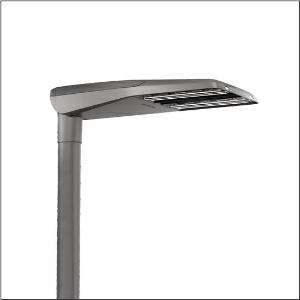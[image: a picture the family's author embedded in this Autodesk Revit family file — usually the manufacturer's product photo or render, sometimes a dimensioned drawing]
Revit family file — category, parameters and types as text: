
# Revit family: streetlight_sl_11_iq_midi___st1_2a_5xc3a51f08me_8c89
name_source: partatom
category: Lighting Fixtures
units: mm (PartAtom-declared; Revit-internal decimal feet)

## family parameters
Cut with Voids When Loaded = No
Host = Face
Light Source = No
Part Type = Normal
Room Calculation Point = No
Round Connector Dimension = Use Diameter
Shared = No

## types (1)
- --- (1 x LED, 18110 lm, 124.7 W, 3000K)
    Apparent Load = 125 VA
    CIE Flux Codes = 32 70 96 100 100
    Color Rendering = 70
    Color Temperature = 3000K
    Default Elevation = 1800 mm
    Description = Streetlight SL 11 iQ midi, mast luminaire, primary light control with 3 zone facetted reflector, of plastic, silver coated, highly specular, primary optical cover: cover, of PMMA, transparent, light distribution: ST1.2a, light emission: direct distribution, primary light characteristic: asymmetric, installation type: post-top, side-entry, LED, High Power LED, rated luminous flux: 18.110lm, luminous efficacy: 145lm/W, light colour: 730, colour temperature: 3000K, control: Street-Remote, optimised constant luminous flux control (CLO 2.0), Desk-Remote (wireless, voltage-free reading and setting of iQ features in the workshop via application-optimized NFC function/RFID function), Light-Fading, Smart-Wire, Night-Set, Lumen-Switch, Temp-Guard, Auto-Match, with cable H07RN-F 5x 1.5mm², mains connection: 230..240V, AC, 50/60Hz, connection cable pre-assembled, cable length: 12,5m, start of lifetime: 125W, end of service life: 132W, reduction: 57W, luminaire housing, of diecast aluminium, powder-coated, Siteco® metallic grey (DB 702S), please order mast flange separately, inclination adjustable without tools: 0°, 5°, 10°, 15° (post-top) | 0°, -5°, -10°, -15° (side-entry), sealing non-destructively replaceable, multi-level sealing system, length: 780mm, width: 376mm, height: 118mm, mast flange for spigot size: 42mm (side-entry): 5XC10008XM4, 60/48mm (side-entry/post-top): 5XC10108XM2, 76/60mm (side-entry/post-top): 5XC10108XM1, equipment: Power, protection rating (complete): IP66, insulation class (complete): insulation class II (safety insulation), certification: CE, ENEC, VDE, impact resistance: IK09, permissible operating ambient temperature for outdoor applications: -25..+50°C, standard-compliant lighting for roads and squares, Environmental Product Declaration (EPD) tested and certified by an independent institute, packaging unit: 1 piece

Light Distribution: ST1.2a
    Height = 118 mm
    Lamp = 1 x LED
    Lamp Light Flux = 18110 lm
    Lamp Power = 124.7 W
    Lamp count = 1
    Length = 780 mm
    Luminous efficacy = 145 lm/W
    Manufacturer = Siteco
    ModVariant = No
    Model = 5XC3A51F08ME
    Number of Poles = 1
    OnlyDefault = Yes
    Power Factor = 1
    Product Name = Streetlight SL 11 iQ midi | ST1.2a
    Product group = mast luminaire | pylon top
    ProductGroupID = 6100
    Protection Class = Protection class II
    Protection Degree = IP 66
    RLX_Detail_Level = 1
    RLX_Emergency_Light_Flux = 0 lm
    RLX_Emergency_Type = 0
    RLX_Emergency_Type_DB = No
    RlxData = <blob elided: 70705 chars, md5=ae799d84>
    Socket = socket
    Standby Power = 0 W
    System Light Flux = 18110 lm
    System Power = 125 W
    Type Comments = factory setting: luminous flux: 100 % | dim-lin: 254 | 557 mA
    Type Image = l_1005960.jpg
    URL = http://relux.com
    VarID = @adj_149703
    Voltage = 0 V
    Weight = 0.00 kg
    Width = 376 mm

## geometry (parser evidence)
native form markers: Blend x4, Sweep x11
no freeform markers — native parametric forms only
